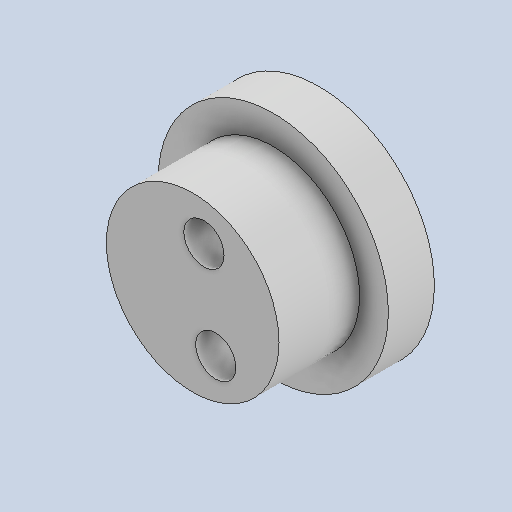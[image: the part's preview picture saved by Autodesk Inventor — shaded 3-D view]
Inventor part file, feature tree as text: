
AUTODESK INVENTOR PART (.ipt)
format: ipt  version: 2023 (Build 270158000, 158)  size: 159,744 bytes
history: native  units: in
note: dims shown in document units (in); Inventor stores cm internally (conversion verified against a paired STEP export)
features: other x3, extrude x2, sketch x2, reference x2
ambient origin geometry x8: Origin, YZ Plane, XZ Plane, XY Plane, X Axis, Y Axis, Z Axis, Center Point
bodies: Solid1 (feature_tree)
feature tree (9):
  extrude  "Extrusion1"  Depth=0.1575in TaperAngle=0.0deg
  extrude  "Extrusion2"  Depth=0.2756in TaperAngle=0.0deg
  sketch  "Sketch1"  dims[d1=0.7874in d2=0.1575in d3=0.0in]
  reference  "Reference1"
  reference  "Reference2"
  sketch  "Sketch2"  dims[d4=0.5906in d5=0.2756in d6=0.0in d7=0.0591in d8=0.315in]
  other  "<userpath>\OneDrive\Documents\Robotics Club\Cycloidal Drive\Drive.iam"
  other  "Drive.iam"
  other  "Shaft-2:1"
